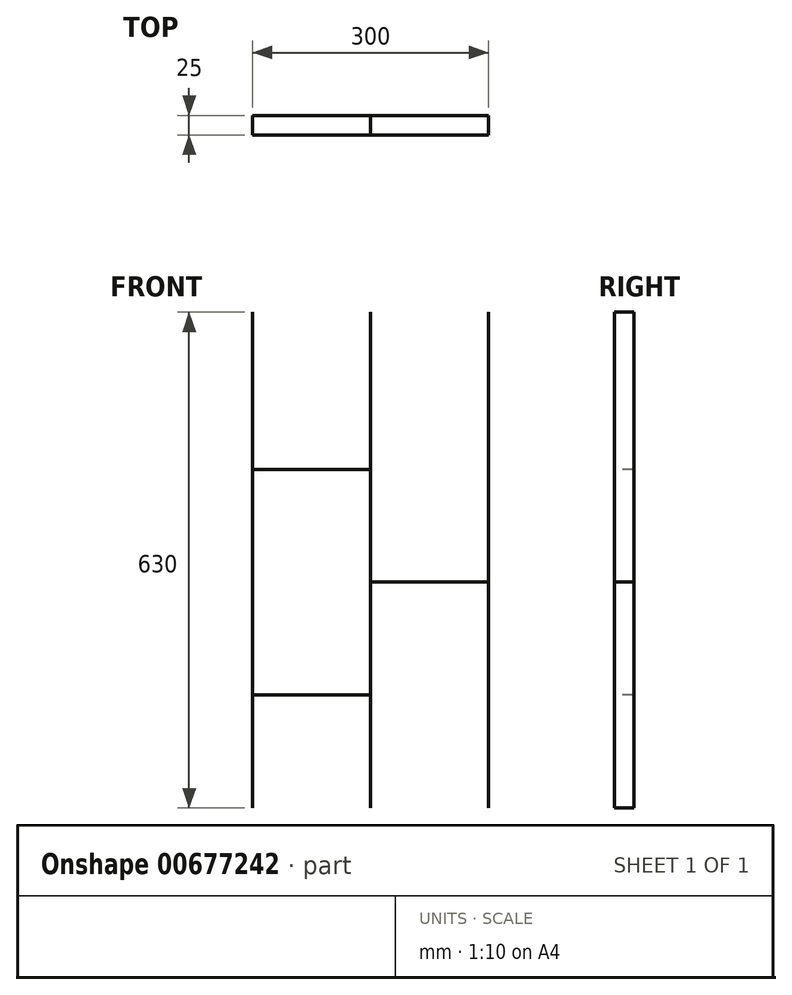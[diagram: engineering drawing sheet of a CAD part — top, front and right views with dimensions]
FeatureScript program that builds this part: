
annotation { "Feature Type Name" : "Feature", "Feature Type Description" : "" }
export const myFeature = defineFeature(function(context is Context, id is Id, definition is map)
    precondition{}
    {
        {
            var Q0;
            Q0=qCreatedBy(makeId("Front.planeOp"),FACE);
            var sketch = newSketch(context, id + "F0", { "sketchPlane" : qUnion([Q0])});
            skLineSegment(sketch, "E0.top", {"start": v(-250, -473.77) * mm, "end": v(250, -473.77) * mm});
            skLineSegment(sketch, "E0.left", {"start": v(-250, 156.23) * mm, "end": v(-250, -473.77) * mm});
            skLineSegment(sketch, "E0.right", {"start": v(250, 156.23) * mm, "end": v(250, -473.77) * mm});
            skLineSegment(sketch, "E1", {"start": v(-150, 156.23) * mm, "end": v(-150, -473.77) * mm});
            skLineSegment(sketch, "E2", {"start": v(0, 156.23) * mm, "end": v(0, -473.77) * mm});
            skLineSegment(sketch, "E3", {"start": v(150, 156.23) * mm, "end": v(150, -473.77) * mm});
            skLineSegment(sketch, "E4", {"start": v(150, -186.77) * mm, "end": v(0, -186.77) * mm});
            skLineSegment(sketch, "E5", {"start": v(-150, -329.77) * mm, "end": v(0, -329.77) * mm});
            skLineSegment(sketch, "E6", {"start": v(-150, -43.77) * mm, "end": v(0, -43.77) * mm});
            skLineSegment(sketch, "E7", {"start": v(-250, 156.23) * mm, "end": v(250, 156.23) * mm});
            skSolve(sketch);
        }
        {
            var Q0;
            Q0=sQuery(id+"F0.wireOp",EDGE,"E6");
            var Q1;
            Q1=sQuery(id+"F0.wireOp",EDGE,"E4");
            var Q2;
            Q2=sQuery(id+"F0.wireOp",EDGE,"E5");
            extrude(context, id + "F1", {"bodyType" : ToolBodyType.SURFACE, "surfaceEntities" : qUnion([Q0, Q1, Q2]), "depth" : 25 * mm, "offsetDistance" : 25 * mm});
        }
        {
            var Q0;
            Q0=sQuery(id+"F0.wireOp",EDGE,"E3");
            var Q1;
            Q1=sQuery(id+"F0.wireOp",EDGE,"E2");
            var Q2;
            Q2=sQuery(id+"F0.wireOp",EDGE,"E1");
            extrude(context, id + "F2", {"bodyType" : ToolBodyType.SURFACE, "surfaceEntities" : qUnion([Q0, Q1, Q2]), "depth" : 25 * mm, "offsetDistance" : 25 * mm});
        }
    });
